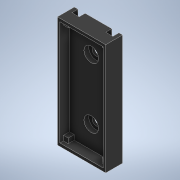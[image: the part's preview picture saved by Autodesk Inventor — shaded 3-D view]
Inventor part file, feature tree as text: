
AUTODESK INVENTOR PART (.ipt)
format: ipt  version: 2021 (Build 250183000, 183)  size: 187,904 bytes
history: native  units: mm
features: projected_geometry x7, extrude x5, sketch x5
ambient origin geometry x8: Origin, YZ Plane, XZ Plane, XY Plane, X Axis, Y Axis, Z Axis, Center Point
bodies: Solid1 (feature_tree)
feature tree (17):
  extrude  "Extrusion1"  Depth=12.5mm
  extrude  "Extrusion2"  Depth=20.0mm
  extrude  "Extrusion3"  Depth=3.0mm TaperAngle=0.0deg
  extrude  "Extrusion4"  Depth=2.0mm TaperAngle=0.0deg
  extrude  "Extrusion5"  Depth=18.0mm
  sketch  "Sketch1"  dims[d0=12.5mm d1=25.0mm]
  sketch  "Sketch2"  dims[d2=3.2mm d3=20.0mm]
  projected_geometry  "Projected Loop1"
  projected_geometry  "Projected Loop2"
  sketch  "Sketch3"  dims[d4=46.0mm d5=3.0mm d6=0.0mm]
  sketch  "Sketch4"  dims[d7=6.0mm d8=2.0mm d9=0.0mm]
  projected_geometry  "Projected Loop3"
  projected_geometry  "Projected Loop4"
  projected_geometry  "Projected Loop5"
  projected_geometry  "Projected Loop6"
  sketch  "Sketch5"  dims[d10=43.5mm d11=18.0mm d12=4.0mm d13=0.0mm d14=2.0mm d15=2.5mm d16=0.0mm d23=2.5mm d24=0.0mm d25=1.5mm d26=3.0mm d27=2.5mm d28=1.5mm]
  projected_geometry  "Projected Loop7"
